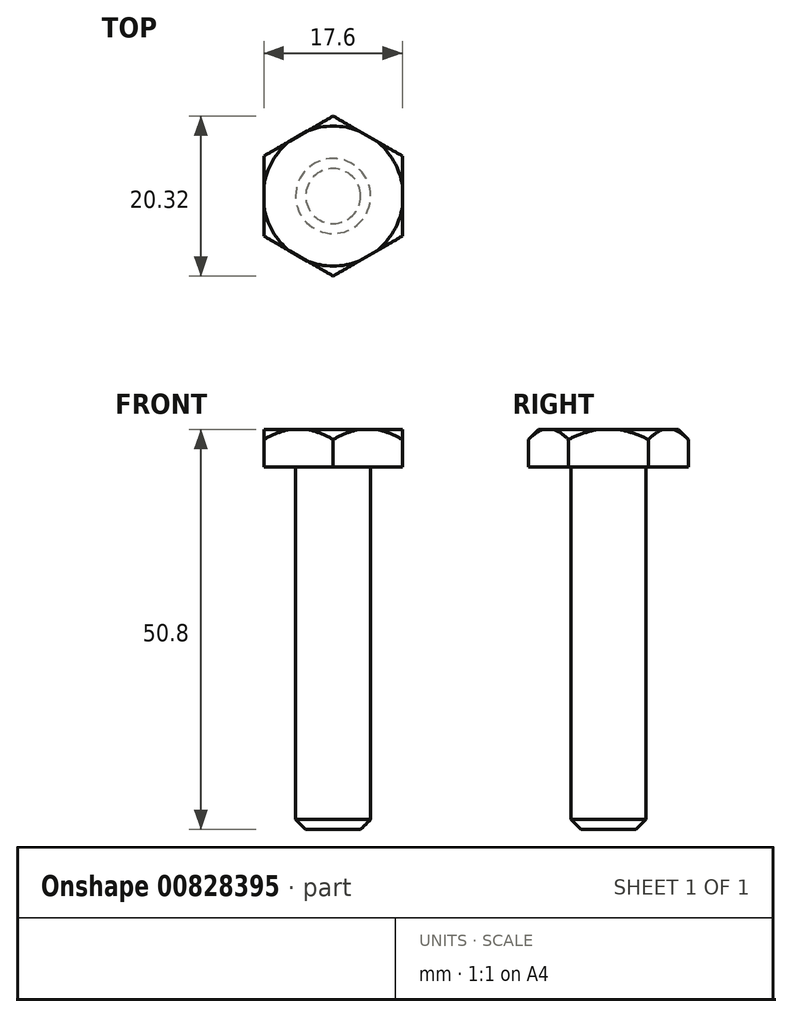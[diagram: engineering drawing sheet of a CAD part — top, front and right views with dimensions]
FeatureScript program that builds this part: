
annotation { "Feature Type Name" : "Feature", "Feature Type Description" : "" }
export const myFeature = defineFeature(function(context is Context, id is Id, definition is map)
    precondition{}
    {
        {
            var Q0;
            Q0=qCreatedBy(makeId("Front.planeOp"),FACE);
            var sketch = newSketch(context, id + "F0", { "sketchPlane" : qUnion([Q0])});
            skLineSegment(sketch, "E0", {"start": v(0, 0) * mm, "end": v(-4.76, 0) * mm});
            skLineSegment(sketch, "E1", {"start": v(-4.76, 0) * mm, "end": v(-4.76, 46.04) * mm});
            skLineSegment(sketch, "E2", {"start": v(-4.76, 46.04) * mm, "end": v(-10.16, 46.04) * mm});
            skLineSegment(sketch, "E3", {"start": v(-10.16, 46.04) * mm, "end": v(-10.16, 50.8) * mm});
            skLineSegment(sketch, "E4", {"start": v(-10.16, 50.8) * mm, "end": v(0, 50.8) * mm});
            skLineSegment(sketch, "E5", {"start": v(0, 0) * mm, "end": v(0, 50.8) * mm, "construction": true});
            skLineSegment(sketch, "E6", {"start": v(0, 50.8) * mm, "end": v(0, 0) * mm});
            skSolve(sketch);
        }
        {
            var Q0;
            Q0 = qSketchRegion(id + "F0", true);
            var Q1;
            Q1=sQuery(id+"F0.wireOp",EDGE,"E6");
            revolve(context, id + "F1", {"surfaceOperationType" : NewSurfaceOperationType.NEW, "entities" : qUnion([Q0]), "axis" : qUnion([Q1]), "revolveType" : RevolveType.FULL});
        }
        {
            var Q0;
            Q0=makeQuery(id+"F1.opRevolve","SWEPT_FACE",FACE,{"disambiguationData":[OSD([sQuery(id+"F0.wireOp",EDGE,"E4")])]});
            var sketch = newSketch(context, id + "F2", { "sketchPlane" : qUnion([Q0])});
            skCircle(sketch, "E7.cCircle", {"center": v(0, 0) * mm, "radius": 8.8 * mm, "construction": true});
            skLineSegment(sketch, "E7.0", {"start": v(0, 10.16) * mm, "end": v(8.8, 5.08) * mm});
            skLineSegment(sketch, "E7.1", {"start": v(8.8, 5.08) * mm, "end": v(8.8, -5.08) * mm});
            skLineSegment(sketch, "E7.2", {"start": v(8.8, -5.08) * mm, "end": v(0, -10.16) * mm});
            skLineSegment(sketch, "E7.3", {"start": v(0, -10.16) * mm, "end": v(-8.8, -5.08) * mm});
            skLineSegment(sketch, "E7.4", {"start": v(-8.8, -5.08) * mm, "end": v(-8.8, 5.08) * mm});
            skLineSegment(sketch, "E7.5", {"start": v(-8.8, 5.08) * mm, "end": v(0, 10.16) * mm});
            skPoint(sketch, "E7.0.midPoint", {"position": v(4.4, 7.62) * mm});
            skCircle(sketch, "E8", {"center": v(0, 0) * mm, "radius": 12.7 * mm});
            skSolve(sketch);
        }
        {
            var Q0;
            Q0 = qSketchRegion(id + "F2", true);
            var Q1;
            Q1=makeQuery(id+"F1.opRevolve","SWEPT_FACE",FACE,{"disambiguationData":[OSD([sQuery(id+"F0.wireOp",EDGE,"E2")])]});
            extrude(context, id + "F3", {"entities" : qUnion([Q0]), "operationType" : NewBodyOperationType.REMOVE, "endBound" : BoundingType.UP_TO_SURFACE, "oppositeDirection" : true, "depth" : 25.4 * mm, "endBoundEntityFace" : qUnion([Q1]), "offsetDistance" : 25.4 * mm});
        }
        {
            var Q0;
            Q0=makeQuery(id+"F1.opRevolve","SWEPT_EDGE",EDGE,{"disambiguationData":[OSD([sQuery(id+"F0.wireOp",EDGE,"E0"),sQuery(id+"F0.wireOp",EDGE,"E1")])]});
            chamfer(context, id + "F4", {"entities" : qUnion([Q0]), "width" : 1.27 * mm, "tangentPropagation" : true});
        }
        {
            var Q0;
            Q0=qCreatedBy(makeId("Right.planeOp"),FACE);
            var sketch = newSketch(context, id + "F5", { "sketchPlane" : qUnion([Q0])});
            skLineSegment(sketch, "E9", {"start": v(10.16, 49.53) * mm, "end": v(8.89, 50.8) * mm});
            skLineSegment(sketch, "E10", {"start": v(8.89, 50.8) * mm, "end": v(10.16, 50.8) * mm});
            skLineSegment(sketch, "E11", {"start": v(10.16, 50.8) * mm, "end": v(10.16, 49.53) * mm});
            skLineSegment(sketch, "E12", {"start": v(0, 0) * mm, "end": v(0, 54.08) * mm, "construction": true});
            skSolve(sketch);
        }
        {
            var Q0;
            Q0 = qSketchRegion(id + "F5", true);
            var Q1;
            Q1=sQuery(id+"F5.wireOp",EDGE,"E12");
            revolve(context, id + "F6", {"operationType" : NewBodyOperationType.REMOVE, "surfaceOperationType" : NewSurfaceOperationType.NEW, "entities" : qUnion([Q0]), "axis" : qUnion([Q1]), "revolveType" : RevolveType.FULL, "oppositeDirection" : true});
        }
    });
